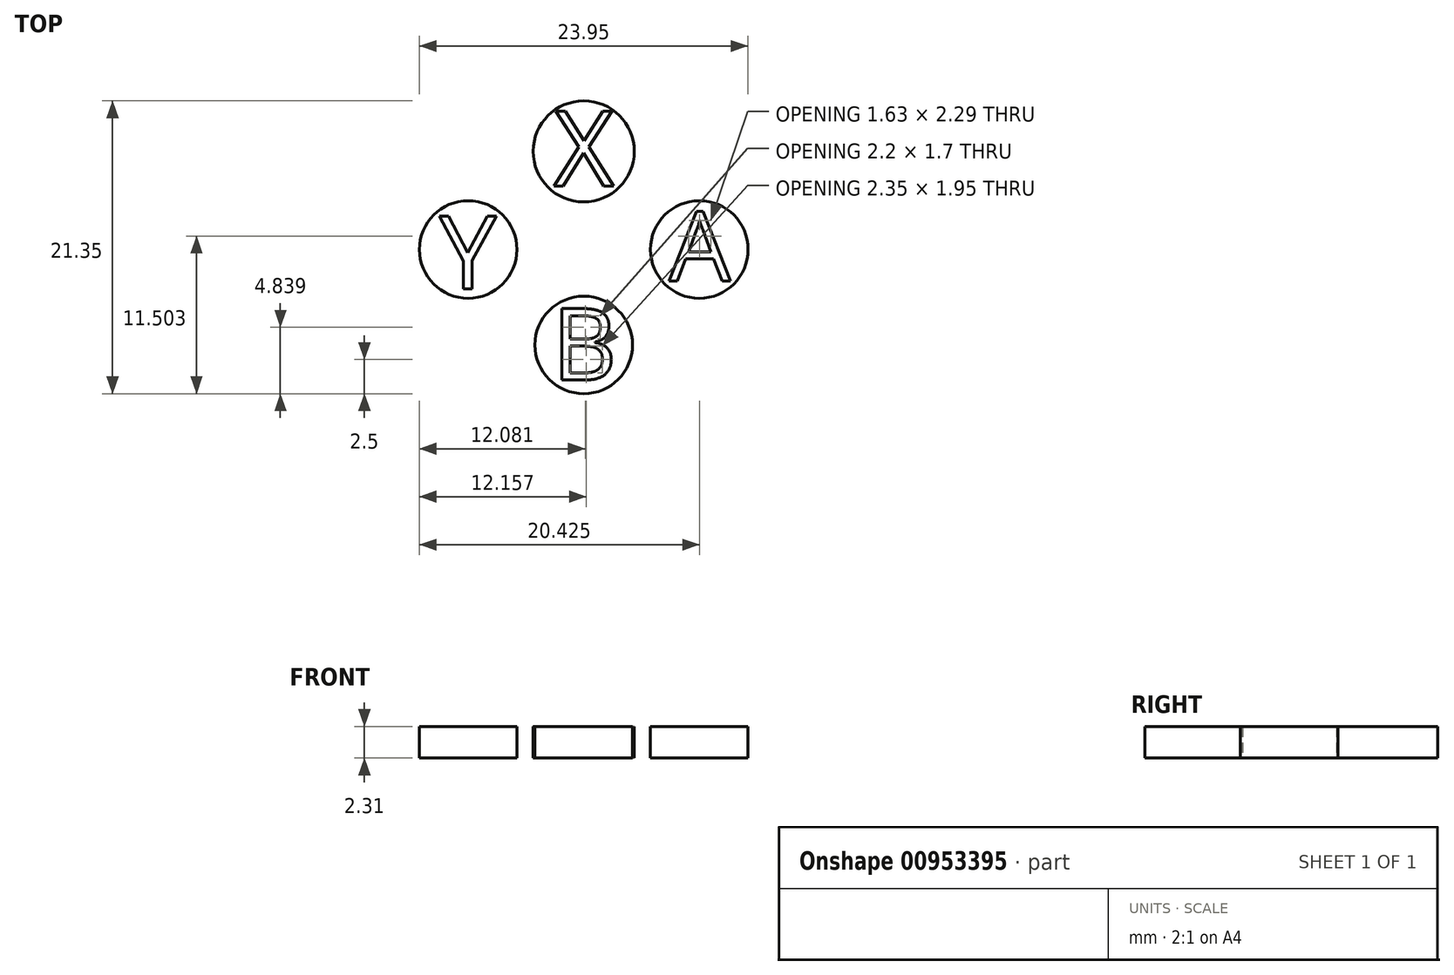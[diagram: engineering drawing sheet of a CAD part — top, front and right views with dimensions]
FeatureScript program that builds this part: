
annotation { "Feature Type Name" : "Feature", "Feature Type Description" : "" }
export const myFeature = defineFeature(function(context is Context, id is Id, definition is map)
    precondition{}
    {
        {
            var Q0;
            Q0=qCreatedBy(makeId("Top.planeOp"),FACE);
            var sketch = newSketch(context, id + "F0", { "sketchPlane" : qUnion([Q0])});
            skCircle(sketch, "E0", {"center": v(-28.45, -20.2) * mm, "radius": 3.68 * mm});
            skCircle(sketch, "E1", {"center": v(-28.45, -34.3) * mm, "radius": 3.56 * mm});
            skCircle(sketch, "E2", {"center": v(-36.87, -27.34) * mm, "radius": 3.56 * mm});
            skCircle(sketch, "E3", {"center": v(-20.03, -27.34) * mm, "radius": 3.56 * mm});
            skSolve(sketch);
        }
        {
            var Q0;
            Q0=qSketchRegion(id+"F0",true);
            extrude(context, id + "F1", {"entities" : qUnion([Q0]), "depth" : 2.3 * mm, "offsetDistance" : 25.4 * mm});
        }
        {
            var Q0;
            Q0=makeQuery(id+"F1.opExtrude","CAP_FACE",FACE,{"disambiguationData":[OSD([sQuery(id+"F0.wireOp",EDGE,"E0")])],"isStart":false});
            var sketch = newSketch(context, id + "F2", { "sketchPlane" : qUnion([Q0])});
            skText(sketch, "E4", { "text": "X", "fontName": "OpenSans-Regular.ttf"});
            const initialGuessF2  = {"E4": [-0.03064, -0.02272, 1, 0, 0.0055]};
            skSetInitialGuess(sketch, initialGuessF2);
            skSolve(sketch);
        }
        {
            var Q0;
            Q0=qSketchRegion(id+"F2",true);
            extrude(context, id + "F3", {"entities" : qUnion([Q0]), "depth" : 0.03 * mm, "offsetDistance" : 25.4 * mm});
        }
        {
            var Q0;
            Q0=makeQuery(id+"F1.opExtrude","CAP_FACE",FACE,{"disambiguationData":[OSD([sQuery(id+"F0.wireOp",EDGE,"E3")])],"isStart":false});
            var sketch = newSketch(context, id + "F4", { "sketchPlane" : qUnion([Q0])});
            skText(sketch, "E5", { "text": "A", "fontName": "OpenSans-Regular.ttf"});
            const initialGuessF4  = {"E5": [-0.02223, -0.02963, 1, 0, 0.00508]};
            skSetInitialGuess(sketch, initialGuessF4);
            skSolve(sketch);
        }
        {
            var Q0;
            Q0=qSketchRegion(id+"F4",true);
            extrude(context, id + "F5", {"entities" : qUnion([Q0]), "depth" : 0.03 * mm, "offsetDistance" : 25.4 * mm});
        }
        {
            var Q0;
            Q0=makeQuery(id+"F1.opExtrude","CAP_FACE",FACE,{"disambiguationData":[OSD([sQuery(id+"F0.wireOp",EDGE,"E2")])],"isStart":false});
            var sketch = newSketch(context, id + "F6", { "sketchPlane" : qUnion([Q0])});
            skText(sketch, "E6", { "text": "Y", "fontName": "OpenSans-Regular.ttf"});
            const initialGuessF6  = {"E6": [-0.03897, -0.03022, 1, 0, 0.00535]};
            skSetInitialGuess(sketch, initialGuessF6);
            skSolve(sketch);
        }
        {
            var Q0;
            Q0=qSketchRegion(id+"F6",true);
            extrude(context, id + "F7", {"entities" : qUnion([Q0]), "depth" : 0.03 * mm, "offsetDistance" : 25.4 * mm});
        }
        {
            var Q0;
            Q0=makeQuery(id+"F1.opExtrude","CAP_FACE",FACE,{"disambiguationData":[OSD([sQuery(id+"F0.wireOp",EDGE,"E1")])],"isStart":false});
            var sketch = newSketch(context, id + "F8", { "sketchPlane" : qUnion([Q0])});
            skText(sketch, "E7", { "text": "B", "fontName": "OpenSans-Regular.ttf"});
            const initialGuessF8  = {"E7": [-0.03076, -0.03685, 1, 0, 0.00525]};
            skSetInitialGuess(sketch, initialGuessF8);
            skSolve(sketch);
        }
        {
            var Q0;
            Q0=qSketchRegion(id+"F8",true);
            extrude(context, id + "F9", {"entities" : qUnion([Q0]), "depth" : 0.03 * mm, "offsetDistance" : 25.4 * mm});
        }
    });
